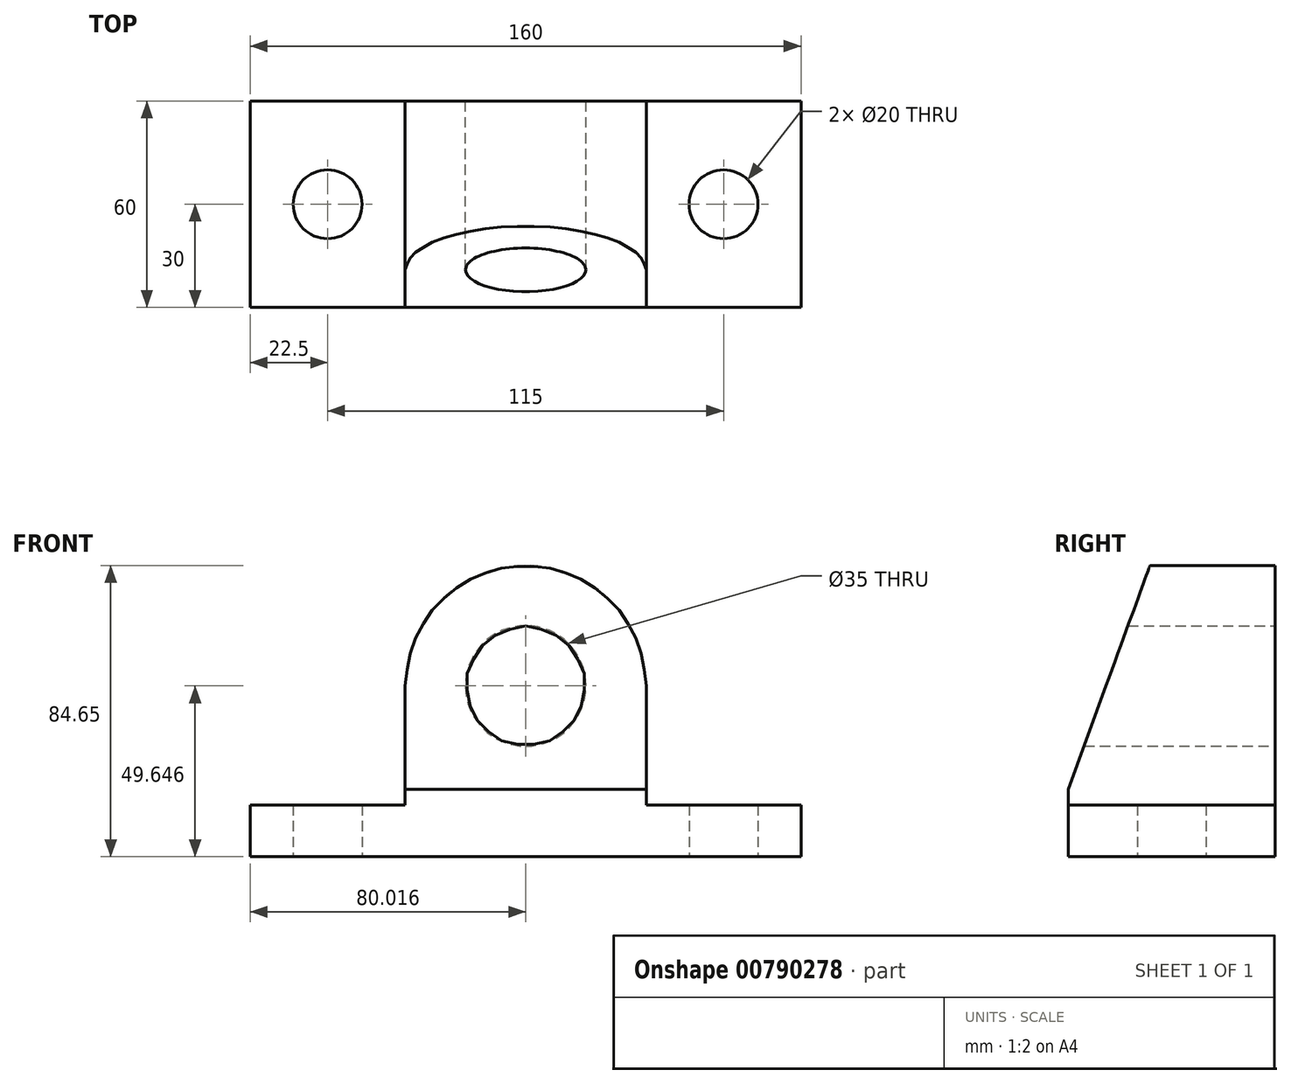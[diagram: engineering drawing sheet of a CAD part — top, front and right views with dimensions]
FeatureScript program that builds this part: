
annotation { "Feature Type Name" : "Feature", "Feature Type Description" : "" }
export const myFeature = defineFeature(function(context is Context, id is Id, definition is map)
    precondition{}
    {
        {
            var Q0;
            Q0=qCreatedBy(makeId("Top.planeOp"),FACE);
            var sketch = newSketch(context, id + "F0", { "sketchPlane" : qUnion([Q0])});
            skLineSegment(sketch, "E0.bottom", {"start": v(-80, 30) * mm, "end": v(80, 30) * mm});
            skLineSegment(sketch, "E0.top", {"start": v(-80, -30) * mm, "end": v(80, -30) * mm});
            skLineSegment(sketch, "E0.left", {"start": v(-80, 30) * mm, "end": v(-80, -30) * mm});
            skLineSegment(sketch, "E0.right", {"start": v(80, 30) * mm, "end": v(80, -30) * mm});
            skCircle(sketch, "E1", {"center": v(-57.5, 0) * mm, "radius": 10 * mm});
            skPoint(sketch, "E1.centerSnap0", {"position": v(-80, 0) * mm});
            skCircle(sketch, "E2", {"center": v(57.5, 0) * mm, "radius": 10 * mm});
            skSolve(sketch);
        }
        {
            var Q0;
            Q0=makeQuery(id+"F0.imprint","IMPRINT",FACE,{"disambiguationData":[TD([[makeQuery(id+"F0.imprint","IMPRINT",EDGE,{"derivedFrom":sQuery(id+"F0.wireOp",EDGE,"E0.bottom")}),-1.0]])]});
            extrude(context, id + "F1", {"entities" : qUnion([Q0]), "depth" : 15 * mm, "offsetDistance" : 25 * mm});
        }
        {
            var Q0;
            Q0=qCreatedBy(makeId("Front.planeOp"),FACE);
            var sketch = newSketch(context, id + "F2", { "sketchPlane" : qUnion([Q0])});
            skCircle(sketch, "E3", {"center": v(0.02, 49.65) * mm, "radius": 17.5 * mm});
            skLineSegment(sketch, "E4.0", {"start": v(-34.98, 49.65) * mm, "end": v(-34.98, 14.65) * mm});
            skLineSegment(sketch, "E5.0", {"start": v(35.02, 54.97) * mm, "end": v(35.02, 14.65) * mm});
            skLineSegment(sketch, "E6", {"start": v(-34.98, 14.65) * mm, "end": v(35.02, 14.65) * mm});
            skLineSegment(sketch, "E7.bottom", {"start": v(-34.98, 49.65) * mm, "end": v(35.02, 49.65) * mm});
            skLineSegment(sketch, "E7.top", {"start": v(-34.98, 84.65) * mm, "end": v(35.02, 84.65) * mm});
            skLineSegment(sketch, "E7.left", {"start": v(-34.98, 49.65) * mm, "end": v(-34.98, 84.65) * mm});
            skLineSegment(sketch, "E7.right", {"start": v(35.02, 49.65) * mm, "end": v(35.02, 84.65) * mm});
            skSolve(sketch);
        }
        {
            var Q0;
            Q0 = qSketchRegion(id + "F2", true);
            var Q1;
            Q1=makeQuery(id+"F2.imprint","IMPRINT",FACE,{"disambiguationData":[TD([[makeQuery(id+"F2.imprint","IMPRINT",EDGE,{"derivedFrom":sQuery(id+"F2.wireOp",EDGE,"E7.top")}),-1.0]])]});
            extrude(context, id + "F3", {"entities" : qUnion([Q0, Q1]), "operationType" : NewBodyOperationType.ADD, "depth" : 30 * mm, "offsetDistance" : 25 * mm, "hasSecondDirection" : true, "secondDirectionOppositeDirection" : true, "secondDirectionDepth" : 30 * mm});
        }
        {
            var Q0;
            Q0=makeQuery(id+"F3.opExtrude","CAP_EDGE",EDGE,{"disambiguationData":[OSD([sQuery(id+"F2.wireOp",EDGE,"E7.top")])],"isStart":false});
            chamfer(context, id + "F4", {"entities" : qUnion([Q0]), "chamferType" : ChamferType.OFFSET_ANGLE, "width" : 65 * mm, "oppositeDirection" : true, "angle" : 20 * degree});
        }
        {
            var Q0;
            Q0=makeQuery(id+"F3.opExtrude","SWEPT_EDGE",EDGE,{"disambiguationData":[OSD([sQuery(id+"F2.wireOp",EDGE,"E7.top"),sQuery(id+"F2.wireOp",EDGE,"E7.right")])]});
            var Q1;
            Q1=makeQuery(id+"F3.opExtrude","SWEPT_EDGE",EDGE,{"disambiguationData":[OSD([sQuery(id+"F2.wireOp",EDGE,"E7.top"),sQuery(id+"F2.wireOp",EDGE,"E7.left")])]});
            fillet(context, id + "F5", {"entities" : qUnion([Q0, Q1]), "radius" : 35 * mm, "tangentPropagation" : true, "allowEdgeOverflow" : false});
        }
    });
